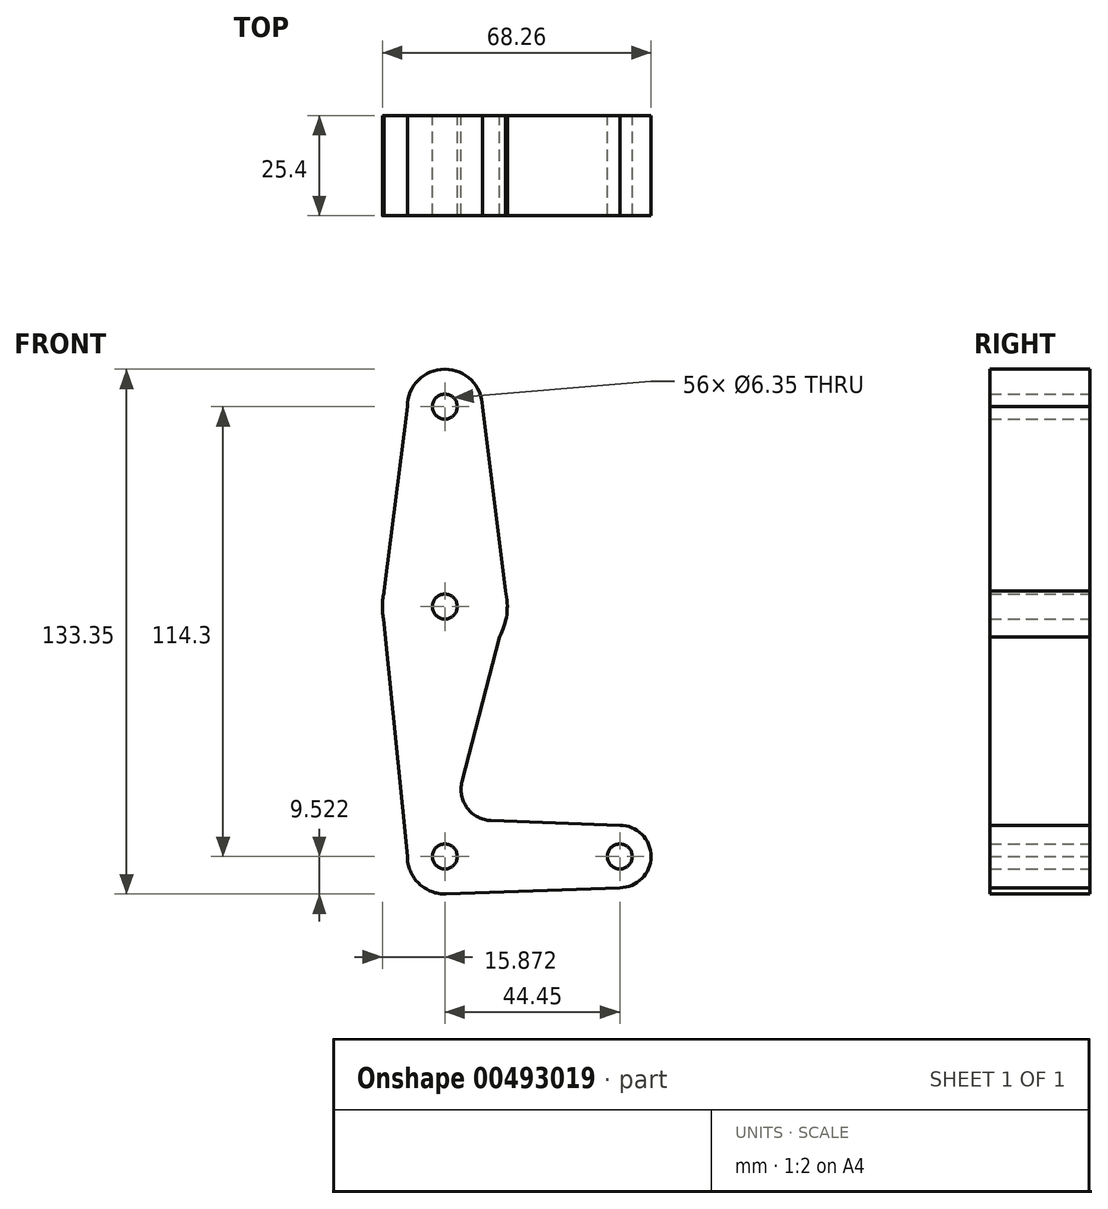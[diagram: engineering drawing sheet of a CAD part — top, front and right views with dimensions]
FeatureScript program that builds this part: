
annotation { "Feature Type Name" : "Feature", "Feature Type Description" : "" }
export const myFeature = defineFeature(function(context is Context, id is Id, definition is map)
    precondition{}
    {
        {
            var Q0;
            Q0=qCreatedBy(makeId("Front.planeOp"),FACE);
            var sketch = newSketch(context, id + "F0", { "sketchPlane" : qUnion([Q0])});
            skLineSegment(sketch, "E0", {"start": v(35.2, 456.71) * mm, "end": v(35.2, 342.41) * mm});
            skLineSegment(sketch, "E1", {"start": v(35.2, 342.41) * mm, "end": v(79.65, 342.41) * mm});
            skCircle(sketch, "E2", {"center": v(35.2, 456.71) * mm, "radius": 9.53 * mm});
            skCircle(sketch, "E3", {"center": v(35.2, 405.91) * mm, "radius": 15.88 * mm});
            skCircle(sketch, "E4", {"center": v(35.2, 342.41) * mm, "radius": 9.53 * mm});
            skCircle(sketch, "E5", {"center": v(79.65, 342.41) * mm, "radius": 7.94 * mm});
            skLineSegment(sketch, "E6", {"start": v(44.73, 456.71) * mm, "end": v(51.08, 405.91) * mm});
            skLineSegment(sketch, "E7", {"start": v(51.08, 405.91) * mm, "end": v(39.58, 361.45) * mm});
            skLineSegment(sketch, "E8", {"start": v(47, 351.52) * mm, "end": v(79.65, 350.35) * mm});
            skLineSegment(sketch, "E9", {"start": v(79.65, 350.35) * mm, "end": v(79.65, 334.47) * mm});
            skLineSegment(sketch, "E10", {"start": v(79.65, 334.47) * mm, "end": v(35.2, 332.88) * mm});
            skLineSegment(sketch, "E11", {"start": v(25.68, 342.41) * mm, "end": v(19.33, 405.91) * mm});
            skLineSegment(sketch, "E12", {"start": v(25.68, 456.71) * mm, "end": v(19.33, 405.91) * mm});
            skCircle(sketch, "E13", {"center": v(35.2, 405.91) * mm, "radius": 3.18 * mm});
            skCircle(sketch, "E14", {"center": v(35.2, 342.41) * mm, "radius": 3.18 * mm});
            skCircle(sketch, "E15", {"center": v(79.65, 342.41) * mm, "radius": 3.18 * mm});
            skCircle(sketch, "E16", {"center": v(35.2, 456.71) * mm, "radius": 3.18 * mm});
            skArc(sketch, "E17.filletArc", {"start": v(39.58, 361.45) * mm, "mid": v(40.9, 354.7) * mm, "end": v(47, 351.52) * mm});
            skSolve(sketch);
        }
        {
            var Q0;
            Q0 = qSketchRegion(id + "F0", true);
            var Q1;
            {var subQ0=sQuery(id+"F0.wireOp",EDGE,"E4");var subQ1=sQuery(id+"F0.wireOp",EDGE,"E0");var subQ2=makeQuery(id+"F0.imprint","INTERSECT",VERTEX,{"derivedFrom":[subQ1,subQ0]});Q1=makeQuery(id+"F0.imprint","IMPRINT",FACE,{"disambiguationData":[TD([[makeQuery(id+"F0.imprint","IMPRINT",EDGE,{"disambiguationData":[TD([[subQ2,-1.0]])],"derivedFrom":subQ1}),1.0]])]});}
            extrude(context, id + "F1", {"entities" : qUnion([Q0, Q1]), "depth" : 25.4 * mm});
        }
    });
